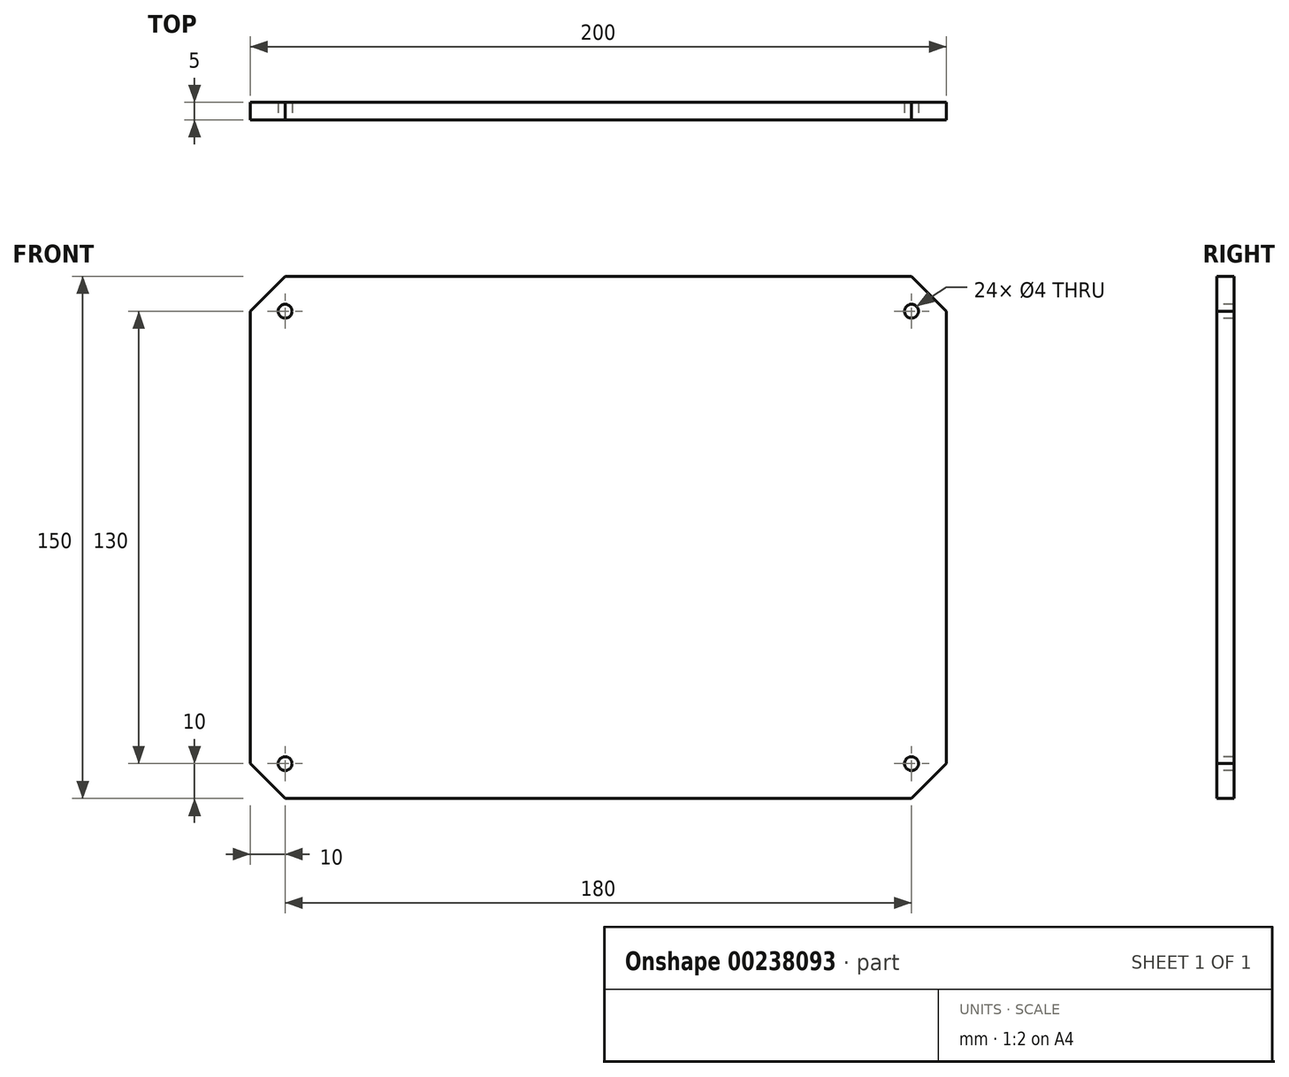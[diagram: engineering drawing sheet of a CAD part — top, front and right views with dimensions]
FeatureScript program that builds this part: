
annotation { "Feature Type Name" : "Feature", "Feature Type Description" : "" }
export const myFeature = defineFeature(function(context is Context, id is Id, definition is map)
    precondition{}
    {
        {
            var Q0;
            Q0=qCreatedBy(makeId("Front.planeOp"),FACE);
            var sketch = newSketch(context, id + "F0", { "sketchPlane" : qUnion([Q0])});
            skLineSegment(sketch, "E0.bottom", {"start": v(100, 75) * mm, "end": v(-100, 75) * mm});
            skLineSegment(sketch, "E0.top", {"start": v(100, -75) * mm, "end": v(-100, -75) * mm});
            skLineSegment(sketch, "E0.left", {"start": v(100, 75) * mm, "end": v(100, -75) * mm});
            skLineSegment(sketch, "E0.right", {"start": v(-100, 75) * mm, "end": v(-100, -75) * mm});
            skPoint(sketch, "E0.middle", {"position": v(0, 0) * mm});
            skSolve(sketch);
        }
        {
            var Q0;
            Q0=makeQuery(id+"F0.imprint","IMPRINT",FACE,{"disambiguationData":[TD([[makeQuery(id+"F0.imprint","IMPRINT",EDGE,{"derivedFrom":sQuery(id+"F0.wireOp",EDGE,"E0.bottom")}),1.0]])]});
            extrude(context, id + "F1", {"entities" : qUnion([Q0]), "depth" : 5 * mm});
        }
        {
            var Q0;
            Q0=makeQuery(id+"F1.opExtrude","SWEPT_EDGE",EDGE,{"disambiguationData":[OSD([sQuery(id+"F0.wireOp",EDGE,"E0.bottom"),sQuery(id+"F0.wireOp",EDGE,"E0.right")])]});
            var Q1;
            Q1=makeQuery(id+"F1.opExtrude","SWEPT_EDGE",EDGE,{"disambiguationData":[OSD([sQuery(id+"F0.wireOp",EDGE,"E0.bottom"),sQuery(id+"F0.wireOp",EDGE,"E0.left")])]});
            var Q2;
            Q2=makeQuery(id+"F1.opExtrude","SWEPT_EDGE",EDGE,{"disambiguationData":[OSD([sQuery(id+"F0.wireOp",EDGE,"E0.top"),sQuery(id+"F0.wireOp",EDGE,"E0.right")])]});
            var Q3;
            Q3=makeQuery(id+"F1.opExtrude","SWEPT_EDGE",EDGE,{"disambiguationData":[OSD([sQuery(id+"F0.wireOp",EDGE,"E0.top"),sQuery(id+"F0.wireOp",EDGE,"E0.left")])]});
            chamfer(context, id + "F2", {"entities" : qUnion([Q0, Q1, Q2, Q3]), "width" : 10 * mm, "tangentPropagation" : true});
        }
        {
            var Q0;
            Q0=makeQuery(id+"F1.opExtrude","CAP_FACE",FACE,{"disambiguationData":[OSD([sQuery(id+"F0.wireOp",EDGE,"E0.bottom"),sQuery(id+"F0.wireOp",EDGE,"E0.top"),sQuery(id+"F0.wireOp",EDGE,"E0.left"),sQuery(id+"F0.wireOp",EDGE,"E0.right")])],"isStart":false});
            var sketch = newSketch(context, id + "F3", { "sketchPlane" : qUnion([Q0])});
            skLineSegment(sketch, "E1.bottom", {"start": v(90, -65) * mm, "end": v(-90, -65) * mm});
            skLineSegment(sketch, "E1.top", {"start": v(90, 65) * mm, "end": v(-90, 65) * mm});
            skLineSegment(sketch, "E1.left", {"start": v(90, -65) * mm, "end": v(90, 65) * mm});
            skLineSegment(sketch, "E1.right", {"start": v(-90, -65) * mm, "end": v(-90, 65) * mm});
            skPoint(sketch, "E1.middle", {"position": v(0, 0) * mm});
            skSolve(sketch);
        }
        {
            var Q0;
            Q0=sQuery(id+"F3.wireOp",VERTEX,"E1.bottom.start");
            var Q1;
            Q1=sQuery(id+"F3.wireOp",VERTEX,"E1.right.start");
            var Q2;
            Q2=sQuery(id+"F3.wireOp",VERTEX,"E1.top.end");
            var Q3;
            Q3=sQuery(id+"F3.wireOp",VERTEX,"E1.left.end");
            var Q4;
            Q4=makeQuery(id+"F1.opExtrude","SWEPT_BODY",BODY,{"disambiguationData":[OSD([sQuery(id+"F0.wireOp",EDGE,"E0.bottom"),sQuery(id+"F0.wireOp",EDGE,"E0.top"),sQuery(id+"F0.wireOp",EDGE,"E0.left"),sQuery(id+"F0.wireOp",EDGE,"E0.right")])]});
            hole(context, id + "F4", {"style" : HoleStyle.SIMPLE, "endStyle" : HoleEndStyle.BLIND, "holeDiameter" : 4 * mm, "holeDepth" : 8 * mm, "startFromSketch" : true, "locations" : qUnion([Q0, Q1, Q2, Q3]), "scope" : qUnion([Q4])});
        }
    });
